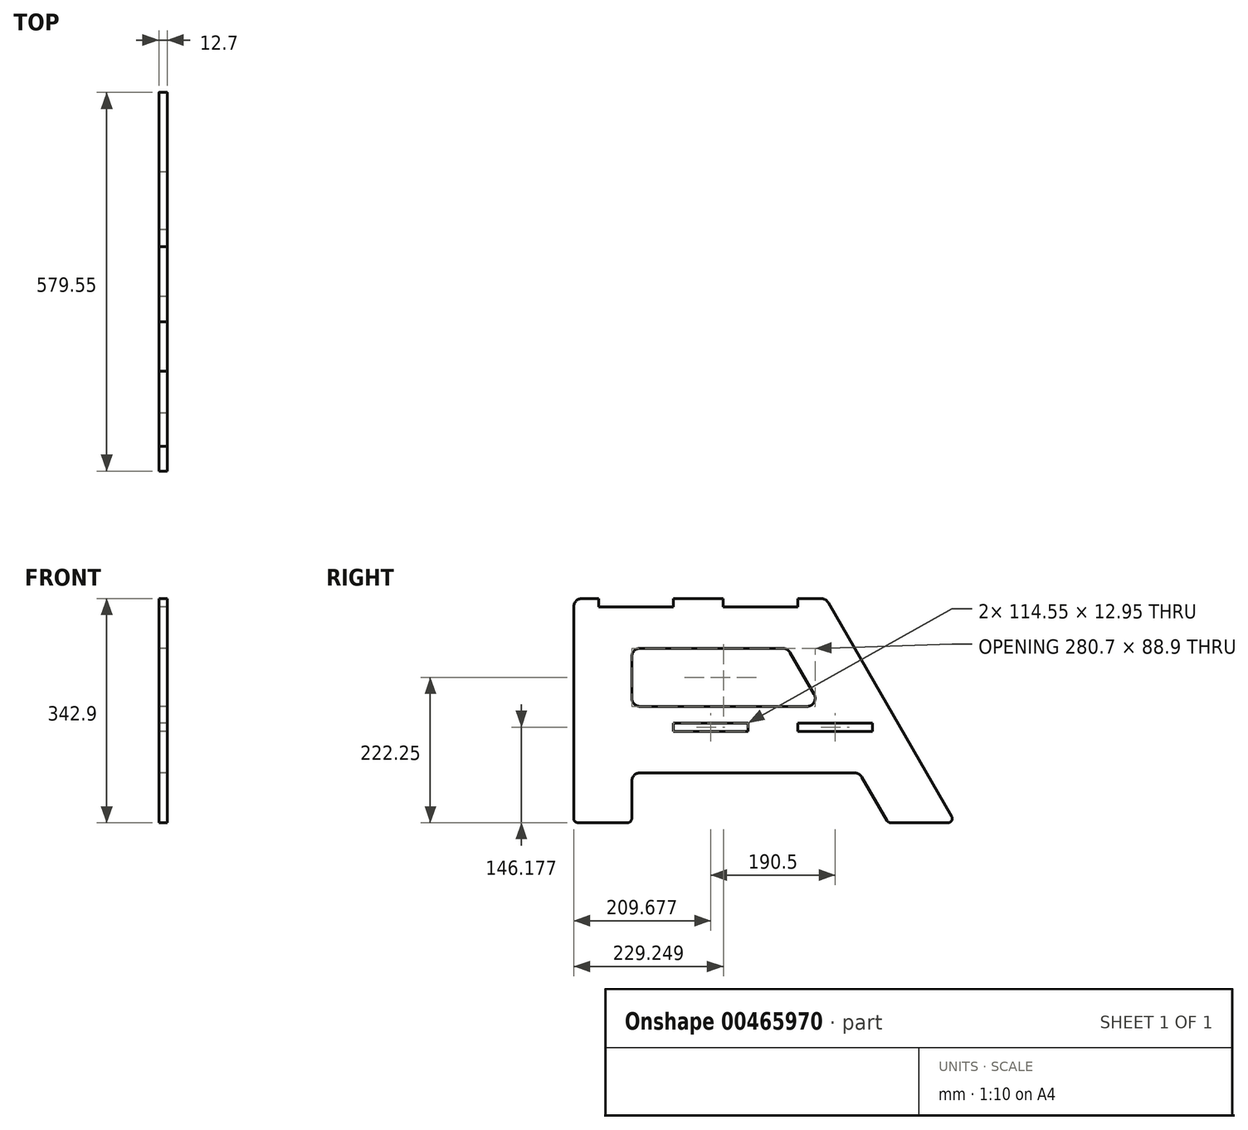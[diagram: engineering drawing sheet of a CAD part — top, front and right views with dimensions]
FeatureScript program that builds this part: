
annotation { "Feature Type Name" : "Feature", "Feature Type Description" : "" }
export const myFeature = defineFeature(function(context is Context, id is Id, definition is map)
    precondition{}
    {
        {
            var Q0;
            Q0=qCreatedBy(makeId("Right.planeOp"),FACE);
            var sketch = newSketch(context, id + "F0", { "sketchPlane" : qUnion([Q0])});
            skLineSegment(sketch, "E0", {"start": v(6.35, 0) * mm, "end": v(82.55, 0) * mm});
            skLineSegment(sketch, "E1", {"start": v(88.9, 6.35) * mm, "end": v(88.9, 63.5) * mm});
            skLineSegment(sketch, "E2", {"start": v(0, 6.35) * mm, "end": v(0, 330.2) * mm});
            skLineSegment(sketch, "E3", {"start": v(12.7, 342.9) * mm, "end": v(38.1, 342.9) * mm});
            skLineSegment(sketch, "E4", {"start": v(38.1, 342.9) * mm, "end": v(38.1, 330.2) * mm});
            skLineSegment(sketch, "E5", {"start": v(38.1, 330.2) * mm, "end": v(152.65, 330.2) * mm});
            skLineSegment(sketch, "E6", {"start": v(343.15, 330.2) * mm, "end": v(343.15, 342.9) * mm});
            skLineSegment(sketch, "E7", {"start": v(343.15, 342.9) * mm, "end": v(378.9, 342.9) * mm});
            skLineSegment(sketch, "E8", {"start": v(389.9, 336.55) * mm, "end": v(578.7, 9.52) * mm});
            skLineSegment(sketch, "E9", {"start": v(573.2, 0) * mm, "end": v(485.21, 0) * mm});
            skLineSegment(sketch, "E10", {"start": v(479.71, 3.17) * mm, "end": v(441.22, 69.85) * mm});
            skLineSegment(sketch, "E11", {"start": v(101.6, 76.2) * mm, "end": v(430.22, 76.2) * mm});
            skLineSegment(sketch, "E12", {"start": v(88.9, 254) * mm, "end": v(88.9, 190.5) * mm});
            skLineSegment(sketch, "E13", {"start": v(152.4, 139.7) * mm, "end": v(266.95, 139.7) * mm});
            skLineSegment(sketch, "E14", {"start": v(367.9, 196.85) * mm, "end": v(331.23, 260.35) * mm});
            skLineSegment(sketch, "E15", {"start": v(320.24, 266.7) * mm, "end": v(101.6, 266.7) * mm});
            skPoint(sketch, "E16.visualSharp", {"position": v(0, 342.9) * mm});
            skArc(sketch, "E16.filletArc", {"start": v(12.7, 342.9) * mm, "mid": v(3.72, 339.18) * mm, "end": v(0, 330.2) * mm});
            skPoint(sketch, "E17.visualSharp", {"position": v(386.23, 342.9) * mm});
            skArc(sketch, "E17.filletArc", {"start": v(389.9, 336.55) * mm, "mid": v(385.24, 341.2) * mm, "end": v(378.9, 342.9) * mm});
            skPoint(sketch, "E18.visualSharp", {"position": v(88.9, 266.7) * mm});
            skArc(sketch, "E18.filletArc", {"start": v(101.6, 266.7) * mm, "mid": v(92.62, 262.98) * mm, "end": v(88.9, 254) * mm});
            skPoint(sketch, "E19.visualSharp", {"position": v(327.57, 266.7) * mm});
            skArc(sketch, "E19.filletArc", {"start": v(331.23, 260.35) * mm, "mid": v(326.59, 265) * mm, "end": v(320.24, 266.7) * mm});
            skPoint(sketch, "E20.visualSharp", {"position": v(88.9, 76.2) * mm});
            skArc(sketch, "E20.filletArc", {"start": v(101.6, 76.2) * mm, "mid": v(92.62, 72.48) * mm, "end": v(88.9, 63.5) * mm});
            skPoint(sketch, "E21.visualSharp", {"position": v(437.55, 76.2) * mm});
            skArc(sketch, "E21.filletArc", {"start": v(441.22, 69.85) * mm, "mid": v(436.57, 74.5) * mm, "end": v(430.22, 76.2) * mm});
            skLineSegment(sketch, "E22", {"start": v(152.65, 330.2) * mm, "end": v(152.65, 342.9) * mm});
            skLineSegment(sketch, "E23", {"start": v(152.65, 342.9) * mm, "end": v(228.6, 342.9) * mm});
            skLineSegment(sketch, "E24", {"start": v(228.6, 342.9) * mm, "end": v(228.6, 330.2) * mm});
            skLineSegment(sketch, "E25.trimOffspring", {"start": v(228.6, 330.2) * mm, "end": v(343.15, 330.2) * mm});
            skLineSegment(sketch, "E26", {"start": v(266.95, 139.7) * mm, "end": v(266.95, 152.65) * mm});
            skLineSegment(sketch, "E27", {"start": v(342.9, 152.65) * mm, "end": v(342.9, 139.7) * mm});
            skLineSegment(sketch, "E28.trimOffspring", {"start": v(342.9, 139.7) * mm, "end": v(457.45, 139.7) * mm});
            skLineSegment(sketch, "E29", {"start": v(152.4, 139.7) * mm, "end": v(152.4, 152.65) * mm});
            skLineSegment(sketch, "E30", {"start": v(457.45, 152.65) * mm, "end": v(457.45, 139.7) * mm});
            skLineSegment(sketch, "E31", {"start": v(356.9, 177.8) * mm, "end": v(101.6, 177.8) * mm});
            skLineSegment(sketch, "E32", {"start": v(457.45, 152.65) * mm, "end": v(342.9, 152.65) * mm});
            skLineSegment(sketch, "E33", {"start": v(266.95, 152.65) * mm, "end": v(152.4, 152.65) * mm});
            skArc(sketch, "E34.filletArc", {"start": v(356.9, 177.8) * mm, "mid": v(367.9, 184.15) * mm, "end": v(367.9, 196.85) * mm});
            skPoint(sketch, "E35.visualSharp", {"position": v(88.9, 177.8) * mm});
            skArc(sketch, "E35.filletArc", {"start": v(88.9, 190.5) * mm, "mid": v(92.62, 181.52) * mm, "end": v(101.6, 177.8) * mm});
            skPoint(sketch, "E36.visualSharp", {"position": v(584.2, 0) * mm});
            skArc(sketch, "E36.filletArc", {"start": v(573.2, 0) * mm, "mid": v(578.7, 3.17) * mm, "end": v(578.7, 9.52) * mm});
            skPoint(sketch, "E37.visualSharp", {"position": v(481.55, 0) * mm});
            skArc(sketch, "E37.filletArc", {"start": v(479.71, 3.17) * mm, "mid": v(482.04, 0.85) * mm, "end": v(485.21, 0) * mm});
            skPoint(sketch, "E38.visualSharp", {"position": v(88.9, 0) * mm});
            skArc(sketch, "E38.filletArc", {"start": v(82.55, 0) * mm, "mid": v(87.04, 1.86) * mm, "end": v(88.9, 6.35) * mm});
            skPoint(sketch, "E39.visualSharp", {"position": v(0, 0) * mm});
            skArc(sketch, "E39.filletArc", {"start": v(0, 6.35) * mm, "mid": v(1.86, 1.86) * mm, "end": v(6.35, 0) * mm});
            skSolve(sketch);
        }
        {
            var Q0;
            Q0=makeQuery(id+"F0.imprint","IMPRINT",FACE,{"disambiguationData":[TD([[makeQuery(id+"F0.imprint","IMPRINT",EDGE,{"derivedFrom":sQuery(id+"F0.wireOp",EDGE,"E0")}),1.0]])]});
            extrude(context, id + "F1", {"entities" : qUnion([Q0]), "depth" : 12.7 * mm});
        }
    });
